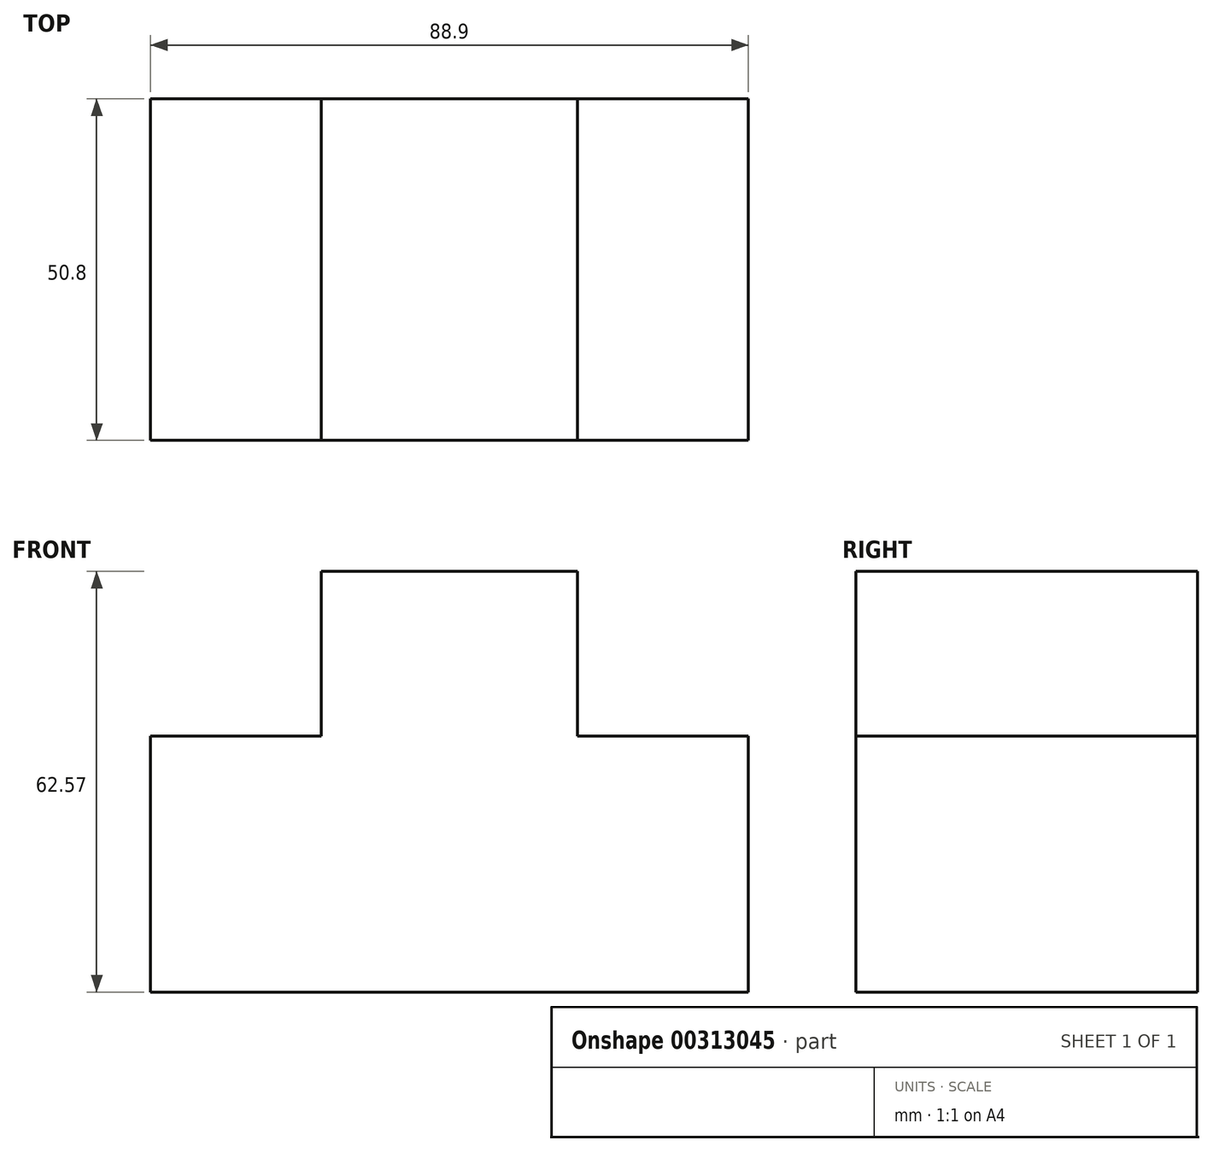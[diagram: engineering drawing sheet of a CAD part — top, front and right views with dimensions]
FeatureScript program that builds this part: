
annotation { "Feature Type Name" : "Feature", "Feature Type Description" : "" }
export const myFeature = defineFeature(function(context is Context, id is Id, definition is map)
    precondition{}
    {
        {
            var Q0;
            Q0=qCreatedBy(makeId("Front.planeOp"),FACE);
            var sketch = newSketch(context, id + "F0", { "sketchPlane" : qUnion([Q0])});
            skLineSegment(sketch, "E0", {"start": v(49.24, -48.12) * mm, "end": v(49.24, -10.02) * mm});
            skLineSegment(sketch, "E1", {"start": v(49.24, -10.02) * mm, "end": v(23.84, -10.02) * mm});
            skLineSegment(sketch, "E2", {"start": v(23.84, -10.02) * mm, "end": v(23.84, 14.45) * mm});
            skLineSegment(sketch, "E3", {"start": v(23.84, 14.45) * mm, "end": v(-14.26, 14.45) * mm});
            skLineSegment(sketch, "E4", {"start": v(-14.26, 14.45) * mm, "end": v(-14.26, -10.02) * mm});
            skLineSegment(sketch, "E5", {"start": v(-14.26, -10.02) * mm, "end": v(-39.66, -10.02) * mm});
            skLineSegment(sketch, "E6", {"start": v(-39.66, -10.02) * mm, "end": v(-39.66, -48.12) * mm});
            skLineSegment(sketch, "E7", {"start": v(-39.66, -48.12) * mm, "end": v(49.24, -48.12) * mm});
            skSolve(sketch);
        }
        {
            var Q0;
            Q0=makeQuery(id+"F0.imprint","IMPRINT",FACE,{"disambiguationData":[TD([[makeQuery(id+"F0.imprint","IMPRINT",EDGE,{"derivedFrom":sQuery(id+"F0.wireOp",EDGE,"E0")}),1.0]])]});
            extrude(context, id + "F1", {"entities" : qUnion([Q0]), "depth" : 50.8 * mm});
        }
    });
